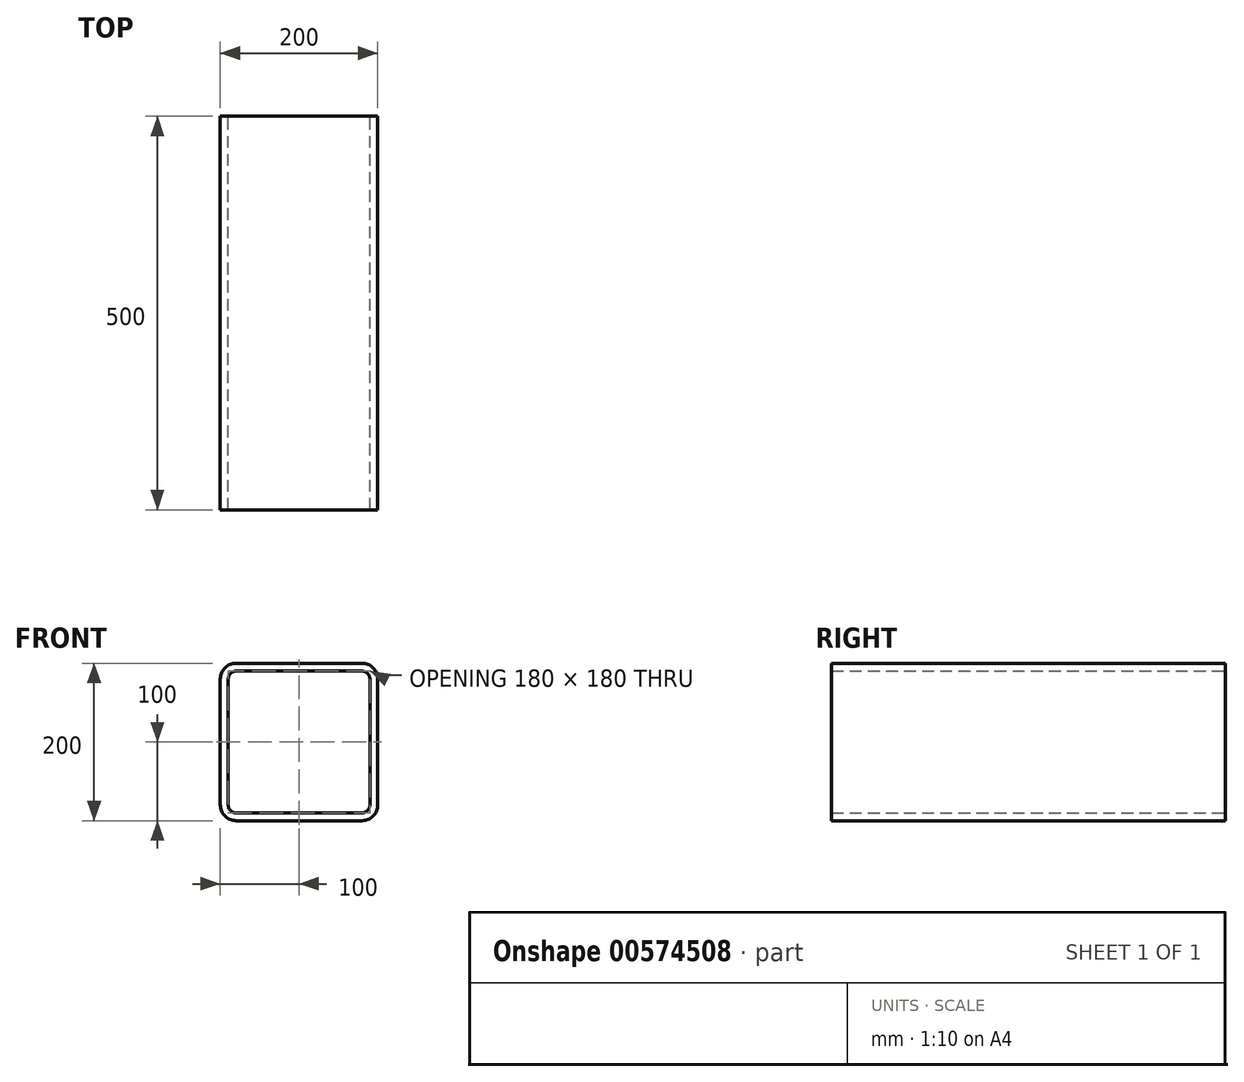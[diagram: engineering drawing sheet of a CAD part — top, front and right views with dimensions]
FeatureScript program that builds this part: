
annotation { "Feature Type Name" : "Feature", "Feature Type Description" : "" }
export const myFeature = defineFeature(function(context is Context, id is Id, definition is map)
    precondition{}
    {
        {
            var Q0;
            Q0=qCreatedBy(makeId("Front.planeOp"),FACE);
            var sketch = newSketch(context, id + "F0", { "sketchPlane" : qUnion([Q0])});
            skLineSegment(sketch, "E0.bottom", {"start": v(80, 100) * mm, "end": v(-80, 100) * mm});
            skLineSegment(sketch, "E0.top", {"start": v(80, -100) * mm, "end": v(-80, -100) * mm});
            skLineSegment(sketch, "E0.left", {"start": v(100, 80) * mm, "end": v(100, -80) * mm});
            skLineSegment(sketch, "E0.right", {"start": v(-100, 80) * mm, "end": v(-100, -80) * mm});
            skPoint(sketch, "E0.middle", {"position": v(0, 0) * mm});
            skLineSegment(sketch, "E1.0", {"start": v(80, 90) * mm, "end": v(-80, 90) * mm});
            skLineSegment(sketch, "E1.1", {"start": v(90, 80) * mm, "end": v(90, -80) * mm});
            skLineSegment(sketch, "E1.2", {"start": v(80, -90) * mm, "end": v(-80, -90) * mm});
            skLineSegment(sketch, "E1.3", {"start": v(-90, 80) * mm, "end": v(-90, -80) * mm});
            skPoint(sketch, "E2.visualSharp", {"position": v(90, 90) * mm});
            skArc(sketch, "E2.filletArc", {"start": v(90, 80) * mm, "mid": v(87.07, 87.07) * mm, "end": v(80, 90) * mm});
            skPoint(sketch, "E3.visualSharp", {"position": v(90, -90) * mm});
            skArc(sketch, "E3.filletArc", {"start": v(80, -90) * mm, "mid": v(87.07, -87.07) * mm, "end": v(90, -80) * mm});
            skPoint(sketch, "E4.visualSharp", {"position": v(-90, -90) * mm});
            skArc(sketch, "E4.filletArc", {"start": v(-90, -80) * mm, "mid": v(-87.07, -87.07) * mm, "end": v(-80, -90) * mm});
            skPoint(sketch, "E5.visualSharp", {"position": v(-90, 90) * mm});
            skArc(sketch, "E5.filletArc", {"start": v(-80, 90) * mm, "mid": v(-87.07, 87.07) * mm, "end": v(-90, 80) * mm});
            skPoint(sketch, "E6.visualSharp", {"position": v(100, 100) * mm});
            skArc(sketch, "E6.filletArc", {"start": v(100, 80) * mm, "mid": v(94.14, 94.14) * mm, "end": v(80, 100) * mm});
            skPoint(sketch, "E7.visualSharp", {"position": v(-100, 100) * mm});
            skArc(sketch, "E7.filletArc", {"start": v(-80, 100) * mm, "mid": v(-94.14, 94.14) * mm, "end": v(-100, 80) * mm});
            skPoint(sketch, "E8.visualSharp", {"position": v(-100, -100) * mm});
            skArc(sketch, "E8.filletArc", {"start": v(-100, -80) * mm, "mid": v(-94.14, -94.14) * mm, "end": v(-80, -100) * mm});
            skPoint(sketch, "E9.visualSharp", {"position": v(100, -100) * mm});
            skArc(sketch, "E9.filletArc", {"start": v(80, -100) * mm, "mid": v(94.14, -94.14) * mm, "end": v(100, -80) * mm});
            skSolve(sketch);
        }
        {
            var Q0;
            Q0 = qSketchRegion(id + "F0", true);
            extrude(context, id + "F1", {"entities" : qUnion([Q0]), "depth" : 500 * mm, "offsetDistance" : 25 * mm});
        }
    });
